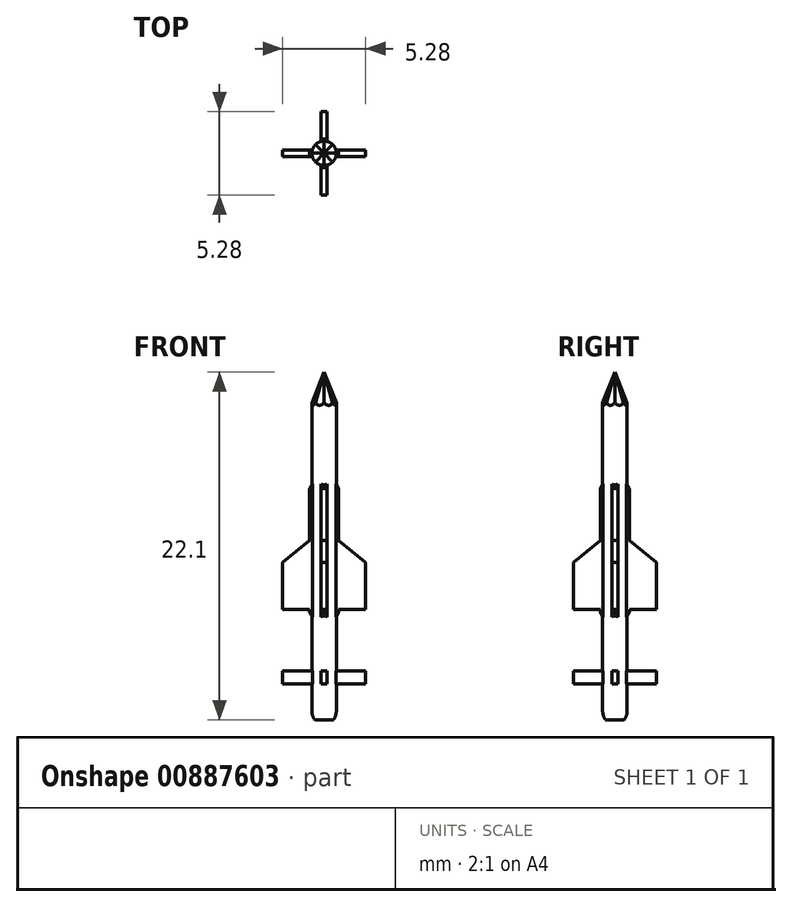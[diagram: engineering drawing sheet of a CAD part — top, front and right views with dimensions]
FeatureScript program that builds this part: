
annotation { "Feature Type Name" : "Feature", "Feature Type Description" : "" }
export const myFeature = defineFeature(function(context is Context, id is Id, definition is map)
    precondition{}
    {
        {
            var Q0;
            Q0=qCreatedBy(makeId("Front.planeOp"),FACE);
            var sketch = newSketch(context, id + "F0", { "sketchPlane" : qUnion([Q0])});
            skLineSegment(sketch, "E0", {"start": v(0, 0) * mm, "end": v(0, 22.15) * mm});
            skLineSegment(sketch, "E1", {"start": v(0.77, 20.14) * mm, "end": v(0.77, 0) * mm});
            skLineSegment(sketch, "E2", {"start": v(0.77, 0) * mm, "end": v(0, 0) * mm});
            skArc(sketch, "E3", {"start": v(0.6, 0) * mm, "mid": v(0.73, 0.26) * mm, "end": v(0.77, 0.56) * mm});
            skLineSegment(sketch, "E4", {"start": v(0.77, 20.14) * mm, "end": v(0, 20.14) * mm});
            skSolve(sketch);
        }
        {
            var Q0;
            {var subQ0=sQuery(id+"F0.wireOp",EDGE,"mrwio9nY-PsAZ-Zbfy-NhIU-sYq0QVbgGXAG");Q0=makeQuery(id+"F0.imprint","IMPRINT",FACE,{"disambiguationData":[TD([[makeQuery(id+"F0.imprint","IMPRINT",EDGE,{"derivedFrom":subQ0}),-1.0]])]});}
            var Q1;
            Q1=makeQuery(id+"F0.imprint","IMPRINT",FACE,{"disambiguationData":[TD([[makeQuery(id+"F0.imprint","IMPRINT",EDGE,{"derivedFrom":sQuery(id+"F0.wireOp",EDGE,"rEedh4zr-IGRr-Hqzj-sDLB-QnI7VE1V64O6.bottom")}),-1.0]])]});
            var Q2;
            Q2=makeQuery(id+"F0.imprint","IMPRINT",FACE,{"disambiguationData":[TD([[makeQuery(id+"F0.imprint","IMPRINT",EDGE,{"derivedFrom":sQuery(id+"F0.wireOp",EDGE,"E0")}),-1.0]])]});
            var Q3;
            Q3=makeQuery(id+"F0.imprint","IMPRINT",FACE,{"disambiguationData":[TD([[makeQuery(id+"F0.imprint","IMPRINT",EDGE,{"derivedFrom":sQuery(id+"F0.wireOp",EDGE,"p5wuz8j9-3HT4-kWwn-DjtP-lJmqTNSXSBJY.bottom")}),-1.0]])]});
            var Q4;
            Q4=sQuery(id+"F0.wireOp",EDGE,"E0");
            revolve(context, id + "F1", {"surfaceOperationType" : NewSurfaceOperationType.NEW, "entities" : qUnion([Q0, Q1, Q2, Q3]), "axis" : qUnion([Q4]), "revolveType" : RevolveType.FULL});
        }
        {
            var Q0;
            Q0=qCreatedBy(makeId("Front.planeOp"),FACE);
            var sketch = newSketch(context, id + "F2", { "sketchPlane" : qUnion([Q0])});
            skLineSegment(sketch, "E5", {"start": v(0, 0) * mm, "end": v(0, 15.58) * mm});
            skLineSegment(sketch, "E6", {"start": v(0.2, 3.13) * mm, "end": v(2.64, 3.13) * mm});
            skLineSegment(sketch, "E7", {"start": v(0.77, 0) * mm, "end": v(0.77, 32.87) * mm, "construction": true});
            skLineSegment(sketch, "E8", {"start": v(0.91, 7.01) * mm, "end": v(2.64, 7.01) * mm});
            skLineSegment(sketch, "E9", {"start": v(2.64, 7.01) * mm, "end": v(2.64, 10) * mm});
            skLineSegment(sketch, "E10", {"start": v(2.64, 2.3) * mm, "end": v(0, 2.3) * mm});
            skLineSegment(sketch, "E11.0", {"start": v(0.77, 0.56) * mm, "end": v(-0.77, 0.56) * mm});
            skLineSegment(sketch, "E12", {"start": v(2.64, 3.13) * mm, "end": v(2.64, 2.3) * mm});
            skLineSegment(sketch, "E13", {"start": v(0.91, 6.84) * mm, "end": v(0.6, 6.3) * mm});
            skLineSegment(sketch, "E14", {"start": v(0.6, 6.3) * mm, "end": v(0.2, 6.3) * mm});
            skLineSegment(sketch, "E15", {"start": v(2.64, 10) * mm, "end": v(0.91, 11.39) * mm});
            skLineSegment(sketch, "E16", {"start": v(0.91, 11.39) * mm, "end": v(0.91, 14.69) * mm});
            skLineSegment(sketch, "E17", {"start": v(0.91, 14.69) * mm, "end": v(0.4, 15.58) * mm});
            skLineSegment(sketch, "E18", {"start": v(0.4, 15.58) * mm, "end": v(0, 15.58) * mm});
            skPoint(sketch, "E19", {"position": v(0.77, 6.6) * mm});
            skPoint(sketch, "E20", {"position": v(0.77, 14.93) * mm});
            skLineSegment(sketch, "E21", {"start": v(0.2, 6.3) * mm, "end": v(0.2, 3.13) * mm});
            skLineSegment(sketch, "E22", {"start": v(0.91, 7.01) * mm, "end": v(0.91, 6.84) * mm});
            skSolve(sketch);
        }
        {
            var Q0;
            Q0=qSketchRegion(id+"F2",true);
            extrude(context, id + "F3", {"entities" : qUnion([Q0]), "operationType" : NewBodyOperationType.ADD, "depth" : .4 * mm, "offsetDistance" : 25 * mm, "symmetric" : true});
        }
        {
            var Q0;
            Q0=makeQuery(id+"F1.opRevolve","SWEPT_BODY",BODY,{"disambiguationData":[OSD([sQuery(id+"F0.wireOp",EDGE,"E0"),sQuery(id+"F0.wireOp",EDGE,"E1"),sQuery(id+"F0.wireOp",EDGE,"E2"),sQuery(id+"F0.wireOp",EDGE,"2EiOItwe-9FNA-eY8p-DkXH-AMy5AHyUmzZA"),sQuery(id+"F0.wireOp",EDGE,"lF35QjYl-MEgV-fRWE-0Yr6-Bt5vS8A7brRf")])]});
            var Q1;
            Q1=makeQuery(id+"F1.opRevolve","SWEPT_FACE",FACE,{"disambiguationData":[OSD([sQuery(id+"F0.wireOp",EDGE,"E1")])]});
            circularPattern(context, id + "F4", {"operationType" : NewBodyOperationType.ADD, "entities" : qUnion([Q0]), "axis" : qUnion([Q1]), "angle" : 360 * degree, "instanceCount" : 4, "equalSpace" : true, "computeTransformsWithoutBuiltin" : true});
        }
        {
            var Q0;
            Q0=makeQuery(id+"F1.opRevolve","SWEPT_FACE",FACE,{"disambiguationData":[OSD([sQuery(id+"F0.wireOp",EDGE,"E4")])]});
            var sketch = newSketch(context, id + "F5", { "sketchPlane" : qUnion([Q0])});
            skCircle(sketch, "E23.cCircle", {"center": v(0, 0) * mm, "radius": 0.77 * mm, "construction": true});
            skLineSegment(sketch, "E23.0", {"start": v(0.55, 0.55) * mm, "end": v(0.77, 0) * mm});
            skLineSegment(sketch, "E23.1", {"start": v(0.77, 0) * mm, "end": v(0.55, -0.55) * mm});
            skLineSegment(sketch, "E23.2", {"start": v(0.55, -0.55) * mm, "end": v(0, -0.77) * mm});
            skLineSegment(sketch, "E23.3", {"start": v(0, -0.77) * mm, "end": v(-0.55, -0.55) * mm});
            skLineSegment(sketch, "E23.4", {"start": v(-0.55, -0.55) * mm, "end": v(-0.77, 0) * mm});
            skLineSegment(sketch, "E23.5", {"start": v(-0.77, 0) * mm, "end": v(-0.55, 0.55) * mm});
            skLineSegment(sketch, "E23.6", {"start": v(-0.55, 0.55) * mm, "end": v(0, 0.77) * mm});
            skLineSegment(sketch, "E23.7", {"start": v(0, 0.77) * mm, "end": v(0.55, 0.55) * mm});
            skCircle(sketch, "E24", {"center": v(0, 0) * mm, "radius": 1.7 * mm});
            skSolve(sketch);
        }
        {
            var Q0;
            Q0=makeQuery(id+"F5.imprint","IMPRINT",FACE,{"disambiguationData":[TD([[makeQuery(id+"F5.imprint","IMPRINT",EDGE,{"derivedFrom":sQuery(id+"F5.wireOp",EDGE,"E23.0")}),-1.0]])]});
            extrude(context, id + "F6", {"entities" : qUnion([Q0]), "operationType" : NewBodyOperationType.ADD, "depth" : 25 * mm, "offsetDistance" : 25 * mm, "hasDraft" : true, "draftAngle" : 20 * degree, "draftPullDirection" : true});
        }
        {
            var Q0;
            Q0 = qSketchRegion(id + "F5", true);
            extrude(context, id + "F7", {"entities" : qUnion([Q0]), "operationType" : NewBodyOperationType.REMOVE, "oppositeDirection" : true, "depth" : 5 * mm, "offsetDistance" : 25 * mm, "hasDraft" : true, "draftAngle" : 20 * degree, "draftPullDirection" : true});
        }
    });
